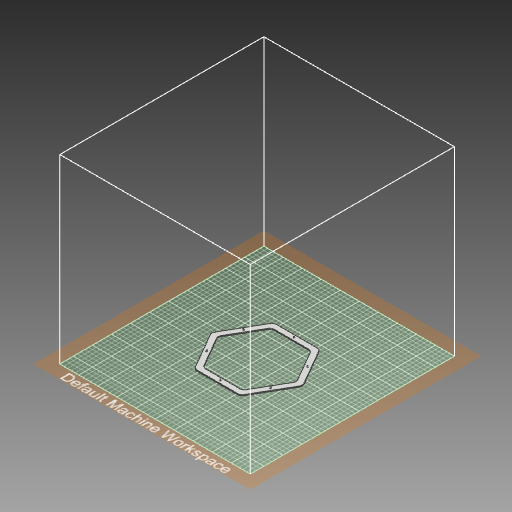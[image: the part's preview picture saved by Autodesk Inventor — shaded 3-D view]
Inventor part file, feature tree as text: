
AUTODESK INVENTOR PART (.ipt)
format: ipt  version: 2019 (Build 230136000, 136)  size: 435,712 bytes
history: native  units: mm
features: extrude x4, sketch x3, projected_geometry x3, fillet x2
ambient origin geometry x8: Origin, YZ Plane, XZ Plane, XY Plane, X Axis, Y Axis, Z Axis, Center Point
bodies: Solid1 (feature_tree)
feature tree (12):
  extrude  "Extrusion1"  Depth=2.0mm TaperAngle=0.0deg
  extrude  "Extrusion6"  Depth=10.0mm
  fillet  "Fillet2"  Radius=10.0mm
  fillet  "Fillet3"  Radius=12.0mm
  extrude  "Extrusion8"  Depth=2.0mm
  extrude  "Extrusion9"  Depth=3.0mm
  sketch  "Sketch1"  dims[d0=175.0mm d1=2.0mm d2=0.0mm]
  sketch  "Sketch7"  dims[d20=7.0mm d21=0.0mm d24=10.0mm d25=10.0mm d26=12.0mm]
  projected_geometry  "Projected Loop7"
  projected_geometry  "Projected Loop9"
  sketch  "Sketch10"  dims[d44=3.0mm d50=2.0mm d51=-1.745329mm d52=3.0mm d53=6.0mm d54=0.7mm d55=0.0mm d56=60.0mm d58=360.0deg]
  projected_geometry  "Projected Loop10"
